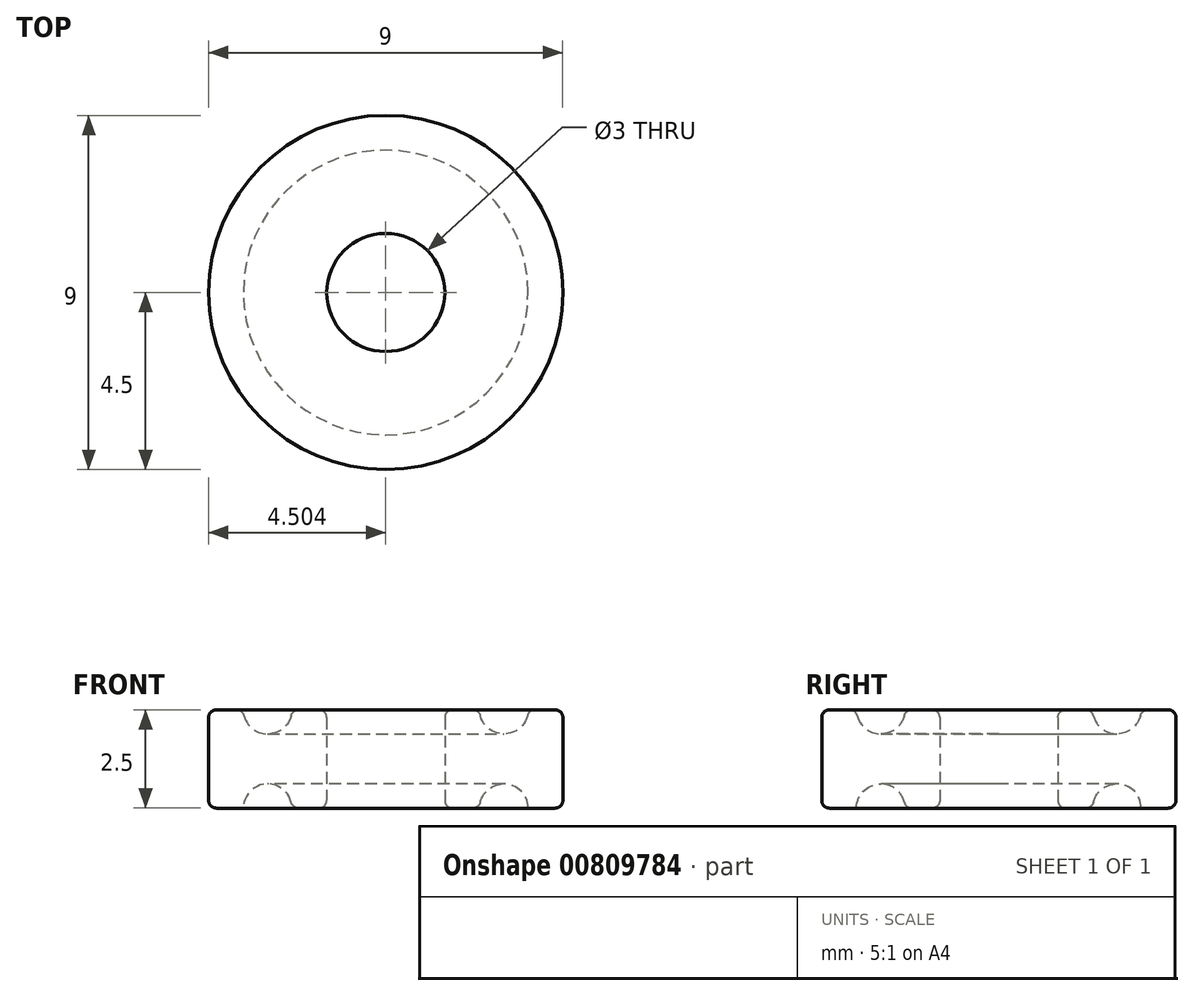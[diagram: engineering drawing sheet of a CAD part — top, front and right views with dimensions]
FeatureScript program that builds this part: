
annotation { "Feature Type Name" : "Feature", "Feature Type Description" : "" }
export const myFeature = defineFeature(function(context is Context, id is Id, definition is map)
    precondition{}
    {
        {
            var Q0;
            Q0=qCreatedBy(makeId("Front.planeOp"),FACE);
            var sketch = newSketch(context, id + "F0", { "sketchPlane" : qUnion([Q0])});
            skLineSegment(sketch, "E0", {"start": v(-95.48, 24.87) * mm, "end": v(-95.48, 27.37) * mm});
            skLineSegment(sketch, "E1", {"start": v(-95.48, 27.37) * mm, "end": v(-94.6, 27.37) * mm});
            skLineSegment(sketch, "E2", {"start": v(-92.48, 24.87) * mm, "end": v(-92.48, 27.37) * mm});
            skLineSegment(sketch, "E3", {"start": v(-84.34, 26.12) * mm, "end": v(-97.62, 26.12) * mm, "construction": true});
            skLineSegment(sketch, "E4", {"start": v(-90.98, 23.44) * mm, "end": v(-90.98, 28.8) * mm, "construction": true});
            skLineSegment(sketch, "E5.trimOffspring", {"start": v(-92.48, 24.87) * mm, "end": v(-93.36, 24.87) * mm});
            skArc(sketch, "E6", {"start": v(-94.6, 27.37) * mm, "mid": v(-93.98, 26.75) * mm, "end": v(-93.36, 27.37) * mm});
            skArc(sketch, "E7", {"start": v(-93.36, 24.87) * mm, "mid": v(-93.98, 25.49) * mm, "end": v(-94.6, 24.87) * mm});
            skLineSegment(sketch, "E8.trimOffspring", {"start": v(-93.36, 27.37) * mm, "end": v(-92.48, 27.37) * mm});
            skLineSegment(sketch, "E9.trimOffspring", {"start": v(-94.6, 24.87) * mm, "end": v(-95.48, 24.87) * mm});
            skSolve(sketch);
        }
        {
            var Q0;
            Q0=makeQuery(id+"F0.imprint","IMPRINT",FACE,{"disambiguationData":[TD([[makeQuery(id+"F0.imprint","IMPRINT",EDGE,{"derivedFrom":sQuery(id+"F0.wireOp",EDGE,"E0")}),-1.0]])]});
            var Q1;
            Q1=sQuery(id+"F0.wireOp",EDGE,"E4");
            revolve(context, id + "F1", {"surfaceOperationType" : NewSurfaceOperationType.NEW, "entities" : qUnion([Q0]), "axis" : qUnion([Q1]), "revolveType" : RevolveType.FULL});
        }
        {
            var Q0;
            Q0=makeQuery(id+"F1.opRevolve","SWEPT_EDGE",EDGE,{"disambiguationData":[OSD([sQuery(id+"F0.wireOp",EDGE,"E0"),sQuery(id+"F0.wireOp",EDGE,"E1")])]});
            var Q1;
            Q1=makeQuery(id+"F1.opRevolve","SWEPT_FACE",FACE,{"disambiguationData":[OSD([sQuery(id+"F0.wireOp",EDGE,"E0")])]});
            var Q2;
            Q2=makeQuery(id+"F1.opRevolve","SWEPT_EDGE",EDGE,{"disambiguationData":[OSD([sQuery(id+"F0.wireOp",EDGE,"E1"),sQuery(id+"F0.wireOp",EDGE,"E2")])]});
            var Q3;
            Q3=makeQuery(id+"F1.opRevolve","SWEPT_EDGE",EDGE,{"disambiguationData":[OSD([sQuery(id+"F0.wireOp",EDGE,"E2"),sQuery(id+"F0.wireOp",EDGE,"E5.trimOffspring")])]});
            var Q4;
            Q4=makeQuery(id+"F1.opRevolve","SWEPT_EDGE",EDGE,{"disambiguationData":[OSD([sQuery(id+"F0.wireOp",EDGE,"E6"),sQuery(id+"F0.wireOp",EDGE,"E8.trimOffspring")])]});
            var Q5;
            Q5=makeQuery(id+"F1.opRevolve","SWEPT_EDGE",EDGE,{"disambiguationData":[OSD([sQuery(id+"F0.wireOp",EDGE,"E5.trimOffspring"),sQuery(id+"F0.wireOp",EDGE,"E7")])]});
            fillet(context, id + "F2", {"entities" : qUnion([Q0, Q1, Q2, Q3, Q4, Q5]), "radius" : 0.2 * mm, "tangentPropagation" : true, "allowEdgeOverflow" : false});
        }
    });
